# Revit family: Haworth_Typical_Parametric_ResideBeside_L_LowStorage
name_source: partatom
category: Furniture Systems
revit_build: Autodesk Revit Architecture 2014 (Build: 20130308_1515(x64)
units: mm (PartAtom-declared; Revit-internal decimal feet)

## types (2) — shared parameters
Actual Storage Depth = 18"
Actual Worksurface Depth = 24"
Angled Double Leg = No
Assembly Code = E2020200
Blade Pull = Yes
Blotter = Yes
Blotter Finish = Haworth _ Polymer _ Snow
Blotter Offset = 15"
Description = Haworth_Typical_Parametric_ResideBeside_L_LowStorage
File Cabinet Finish = Haworth _ Laminate _ Columbian Walnut H-KG
File Drawer Finish = Haworth _ Metal _ Brushed Aluminum
File Pull Finish = Haworth _ Metal _ Brushed Aluminum
Half Worksurface Depth = 12"
Hardware Finish = Haworth _ Metal _ Brushed Aluminum
Hoop Leg = Yes
J Pull = No
Manufacturer = Haworth
Max Height = 74"
Max Storage Length = 72"
Max Worksurface Depth = 30"
Max Worksurface Length = 96"
Maximum Length Storage = 72 in.
Maximum Length Worksurface = 96 in.
Min Storage Length = 48"
Min Worksurface Depth = 24"
Min Worksurface Length = 60"
Minimum Length Storage = 48 in.
Minimum Length Worksurface = 60 in.
Model = Haworth_Typical_Parametric_ResideBeside_L_LowStorage
Offset Screen Center = 1/4"
Revision = 1
Screen = Yes
Screen Finish = Haworth _ Fabric _ Tellure _ Steel 3A-39
Screen Offset = 1/2"
Seat Arm Cap Finish = Haworth _ Paint _ Smoke
Seat Back Upholstery Finish = Haworth _ Fabric _ Zody Mesh _ Comfort MA-002
Seat Cushion Finish = Haworth _ Fabric _ Zinger _ Gravel NI-4
Seat Shell Finish = Haworth _ Metal _ Brushed Aluminum
Seat Support Finish = Haworth _ Paint _ Smoke
Size = Verify Final Dim. w/ Haworth
Storage Middle = 9"
Straight Double Leg = No
Support Offset = 6 1/2"
Sustainability Info = www.haworth.com/en-us/About-Us/Sustainability/Pages/Vision.aspx
Task Chair = Yes
URL = http://haworth.com
URL - Product = http://haworth.com
Warranty = http://haworth.com
Worksurface Depth = 24"
Worksurface Edge Finish = Haworth _ Laminate _ Columbian Walnut H-KG
Worksurface Finish = Haworth _ Laminate _ Columbian Walnut H-KG

## per-type parameters (varying)
| type | Actual Storage Length | Actual Worksurface Length | Chair Location | Screen Length | Storage Length | Worksurface Length |
| 8x6 | 72" | 96" | 39" | 66" | 72" | 96" |
| 5x4 | 48" | 60" | 21" | 30" | 48" | 60" |

## geometry (parser evidence)
native form markers: Blend x31, Sweep x47
no freeform markers — native parametric forms only
